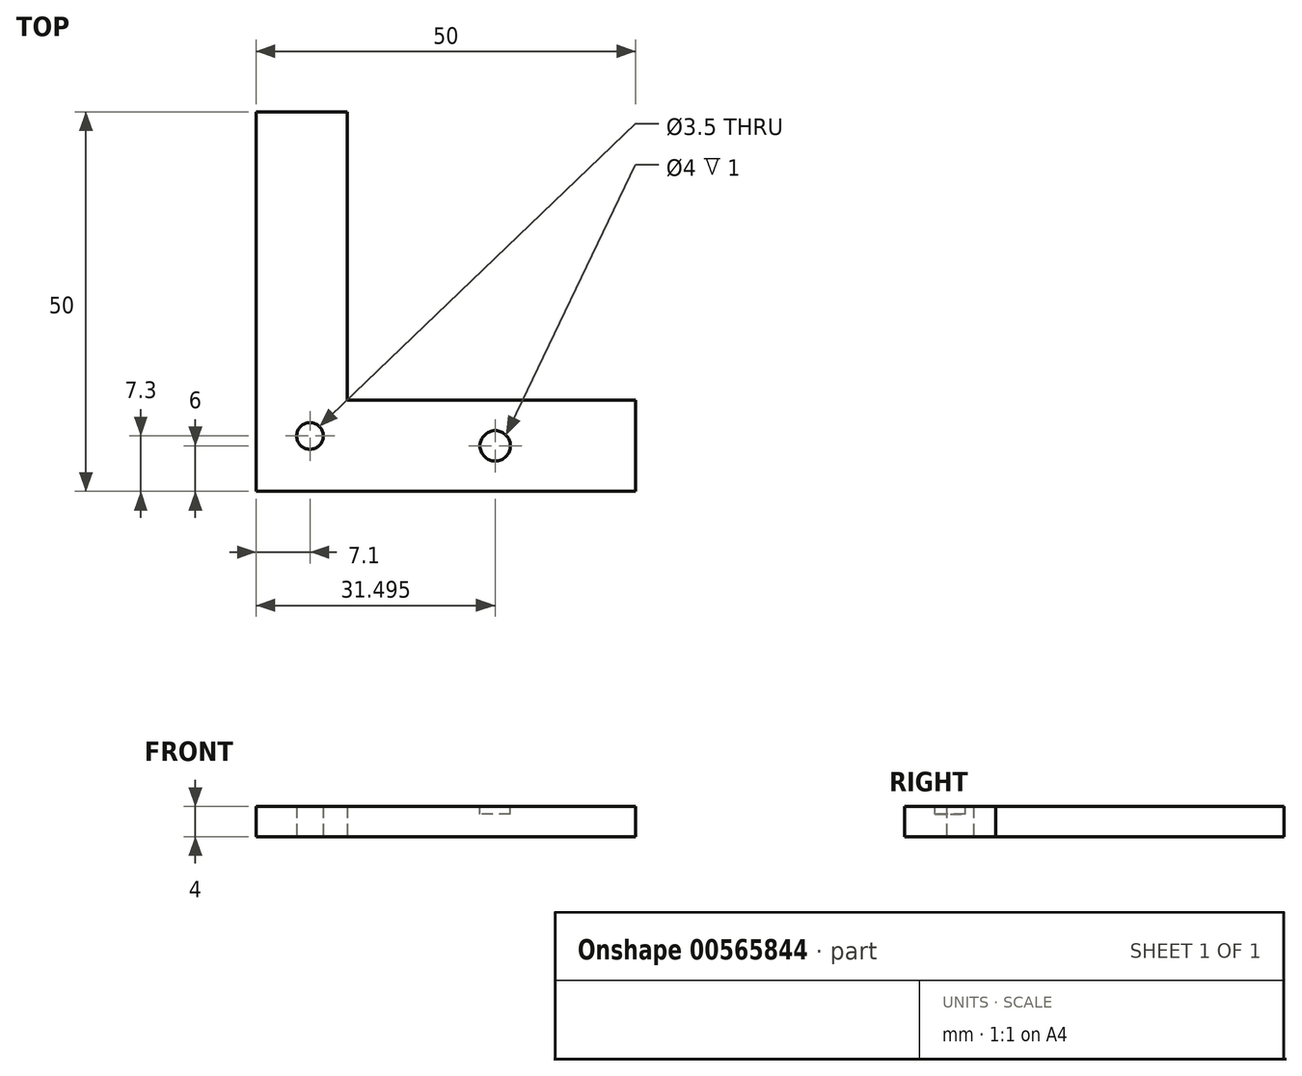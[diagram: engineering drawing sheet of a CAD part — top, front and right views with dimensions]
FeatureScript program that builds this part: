
annotation { "Feature Type Name" : "Feature", "Feature Type Description" : "" }
export const myFeature = defineFeature(function(context is Context, id is Id, definition is map)
    precondition{}
    {
        {
            var Q0;
            Q0=qCreatedBy(makeId("Top.planeOp"),FACE);
            var sketch = newSketch(context, id + "F0", { "sketchPlane" : qUnion([Q0])});
            skLineSegment(sketch, "E0", {"start": v(0, 0) * mm, "end": v(50, 0) * mm});
            skLineSegment(sketch, "E1", {"start": v(50, 0) * mm, "end": v(50, 12) * mm});
            skLineSegment(sketch, "E2", {"start": v(50, 12) * mm, "end": v(12, 12) * mm});
            skLineSegment(sketch, "E3", {"start": v(12, 12) * mm, "end": v(12, 50) * mm});
            skLineSegment(sketch, "E4", {"start": v(12, 50) * mm, "end": v(0, 50) * mm});
            skLineSegment(sketch, "E5", {"start": v(0, 50) * mm, "end": v(0, 0) * mm});
            skCircle(sketch, "E6", {"center": v(7.1, 7.3) * mm, "radius": 1.75 * mm});
            skSolve(sketch);
        }
        {
            var Q0;
            Q0=makeQuery(id+"F0.imprint","IMPRINT",FACE,{"disambiguationData":[TD([[makeQuery(id+"F0.imprint","IMPRINT",EDGE,{"derivedFrom":sQuery(id+"F0.wireOp",EDGE,"E0")}),1.0]])]});
            extrude(context, id + "F1", {"entities" : qUnion([Q0]), "depth" : 4 * mm, "offsetDistance" : 25 * mm});
        }
        {
            var Q0;
            Q0=makeQuery(id+"F1.opExtrude","CAP_FACE",FACE,{"disambiguationData":[OSD([sQuery(id+"F0.wireOp",EDGE,"E0"),sQuery(id+"F0.wireOp",EDGE,"E1"),sQuery(id+"F0.wireOp",EDGE,"E2"),sQuery(id+"F0.wireOp",EDGE,"E3"),sQuery(id+"F0.wireOp",EDGE,"E4"),sQuery(id+"F0.wireOp",EDGE,"E5"),sQuery(id+"F0.wireOp",EDGE,"E6")])],"isStart":false});
            var sketch = newSketch(context, id + "F2", { "sketchPlane" : qUnion([Q0])});
            skCircle(sketch, "E7", {"center": v(31.5, 6) * mm, "radius": 2 * mm});
            skPoint(sketch, "E8.0", {"position": v(50, 6) * mm});
            skSolve(sketch);
        }
        {
            var Q0;
            Q0=makeQuery(id+"F2.imprint","IMPRINT",FACE,{"disambiguationData":[TD([[makeQuery(id+"F2.imprint","IMPRINT",EDGE,{"derivedFrom":sQuery(id+"F2.wireOp",EDGE,"E7")}),1.0]])]});
            extrude(context, id + "F3", {"entities" : qUnion([Q0]), "operationType" : NewBodyOperationType.REMOVE, "oppositeDirection" : true, "depth" : 1 * mm, "offsetDistance" : 25 * mm});
        }
    });
